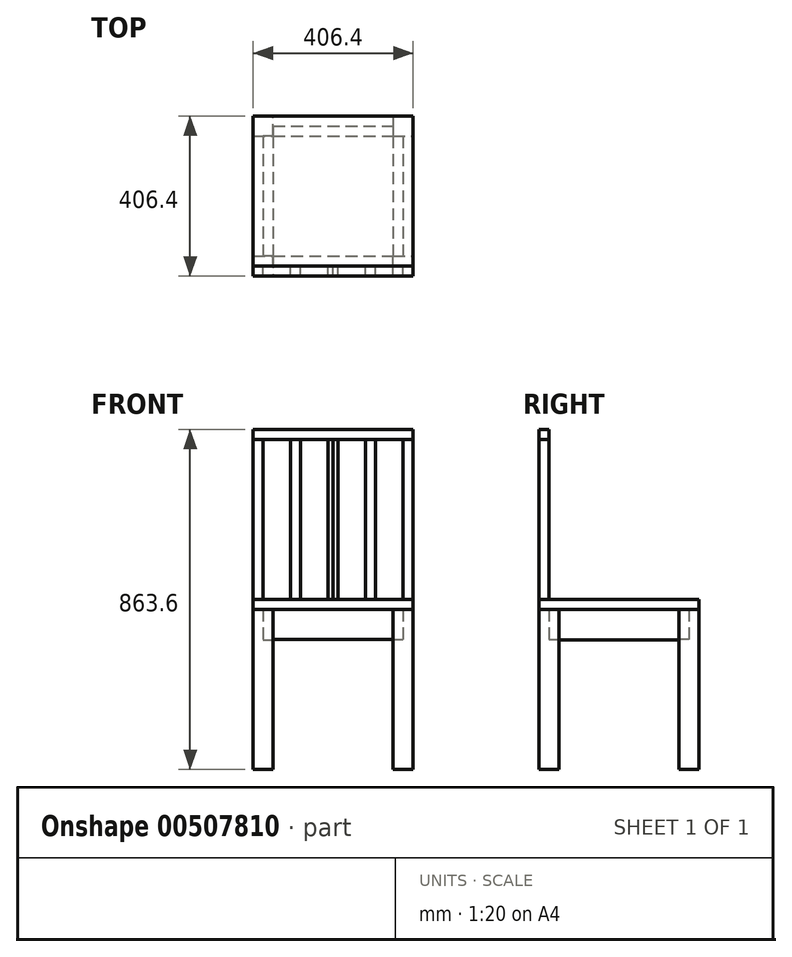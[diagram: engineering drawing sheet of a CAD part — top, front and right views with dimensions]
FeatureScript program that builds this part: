
annotation { "Feature Type Name" : "Feature", "Feature Type Description" : "" }
export const myFeature = defineFeature(function(context is Context, id is Id, definition is map)
    precondition{}
    {
        {
            var Q0;
            Q0=qCreatedBy(makeId("Top.planeOp"),FACE);
            var sketch = newSketch(context, id + "F0", { "sketchPlane" : qUnion([Q0])});
            skLineSegment(sketch, "E0.bottom", {"start": v(0, 0) * mm, "end": v(406.4, 0) * mm});
            skLineSegment(sketch, "E0.top", {"start": v(0, 406.4) * mm, "end": v(406.4, 406.4) * mm});
            skLineSegment(sketch, "E0.left", {"start": v(0, 0) * mm, "end": v(0, 406.4) * mm});
            skLineSegment(sketch, "E0.right", {"start": v(406.4, 0) * mm, "end": v(406.4, 406.4) * mm});
            skPoint(sketch, "E1", {"position": v(0, 50.8) * mm});
            skPoint(sketch, "E2", {"position": v(50.8, 0) * mm});
            skPoint(sketch, "E3", {"position": v(406.4, 50.8) * mm});
            skPoint(sketch, "E4", {"position": v(50.8, 406.4) * mm});
            skPoint(sketch, "E5", {"position": v(0, 355.6) * mm});
            skLineSegment(sketch, "E6", {"start": v(0, 355.6) * mm, "end": v(50.8, 355.6) * mm});
            skLineSegment(sketch, "E7", {"start": v(50.8, 355.6) * mm, "end": v(50.8, 406.4) * mm});
            skPoint(sketch, "E8", {"position": v(355.6, 406.4) * mm});
            skPoint(sketch, "E9", {"position": v(406.4, 355.6) * mm});
            skLineSegment(sketch, "E10", {"start": v(355.6, 406.4) * mm, "end": v(355.6, 355.6) * mm});
            skLineSegment(sketch, "E11", {"start": v(355.6, 355.6) * mm, "end": v(406.4, 355.6) * mm});
            skPoint(sketch, "E12", {"position": v(355.6, 0) * mm});
            skLineSegment(sketch, "E13", {"start": v(355.6, 0) * mm, "end": v(355.6, 50.8) * mm});
            skLineSegment(sketch, "E14", {"start": v(355.6, 50.8) * mm, "end": v(406.4, 50.8) * mm});
            skLineSegment(sketch, "E15", {"start": v(0, 50.8) * mm, "end": v(50.8, 50.8) * mm});
            skLineSegment(sketch, "E16", {"start": v(50.8, 50.8) * mm, "end": v(50.8, 0) * mm});
            skSolve(sketch);
        }
        {
            var Q0;
            {var subQ4=sQuery(id+"F0.wireOp",EDGE,"E15");Q0=makeQuery(id+"F0.imprint","IMPRINT",FACE,{"disambiguationData":[TD([[makeQuery(id+"F0.imprint","IMPRINT",EDGE,{"derivedFrom":subQ4}),-1.0]])]});}
            var Q1;
            {var subQ3=sQuery(id+"F0.wireOp",EDGE,"E13");Q1=makeQuery(id+"F0.imprint","IMPRINT",FACE,{"disambiguationData":[TD([[makeQuery(id+"F0.imprint","IMPRINT",EDGE,{"derivedFrom":subQ3}),-1.0]])]});}
            var Q2;
            {var subQ3=sQuery(id+"F0.wireOp",EDGE,"E10");Q2=makeQuery(id+"F0.imprint","IMPRINT",FACE,{"disambiguationData":[TD([[makeQuery(id+"F0.imprint","IMPRINT",EDGE,{"derivedFrom":subQ3}),1.0]])]});}
            var Q3;
            {var subQ4=sQuery(id+"F0.wireOp",EDGE,"E6");Q3=makeQuery(id+"F0.imprint","IMPRINT",FACE,{"disambiguationData":[TD([[makeQuery(id+"F0.imprint","IMPRINT",EDGE,{"derivedFrom":subQ4}),1.0]])]});}
            extrude(context, id + "F1", {"entities" : qUnion([Q0, Q1, Q2, Q3]), "depth" : 406.4 * mm});
        }
        {
            var Q0;
            Q0=makeQuery(id+"F1.opExtrude","CAP_FACE",FACE,{"disambiguationData":[OSD([sQuery(id+"F0.wireOp",EDGE,"E0.bottom"),sQuery(id+"F0.wireOp",EDGE,"E0.left"),sQuery(id+"F0.wireOp",EDGE,"E15"),sQuery(id+"F0.wireOp",EDGE,"E16")])],"isStart":false});
            var sketch = newSketch(context, id + "F2", { "sketchPlane" : qUnion([Q0])});
            skLineSegment(sketch, "E17.bottom", {"start": v(0, 0) * mm, "end": v(406.4, 0) * mm});
            skLineSegment(sketch, "E17.top", {"start": v(0, 406.4) * mm, "end": v(406.4, 406.4) * mm});
            skLineSegment(sketch, "E17.left", {"start": v(0, 0) * mm, "end": v(0, 406.4) * mm});
            skLineSegment(sketch, "E17.right", {"start": v(406.4, 0) * mm, "end": v(406.4, 406.4) * mm});
            skSolve(sketch);
        }
        {
            var Q0;
            Q0 = qSketchRegion(id + "F2", true);
            extrude(context, id + "F3", {"entities" : qUnion([Q0]), "depth" : 25.4 * mm});
        }
        {
            var Q0;
            Q0=makeQuery(id+"F3.opExtrude","CAP_FACE",FACE,{"disambiguationData":[OSD([sQuery(id+"F2.wireOp",EDGE,"E17.bottom"),sQuery(id+"F2.wireOp",EDGE,"E17.top"),sQuery(id+"F2.wireOp",EDGE,"E17.left"),sQuery(id+"F2.wireOp",EDGE,"E17.right")])],"isStart":false});
            var sketch = newSketch(context, id + "F4", { "sketchPlane" : qUnion([Q0])});
            skLineSegment(sketch, "E18.bottom", {"start": v(0, 0) * mm, "end": v(25.4, 0) * mm});
            skLineSegment(sketch, "E18.top", {"start": v(0, 25.4) * mm, "end": v(25.4, 25.4) * mm});
            skLineSegment(sketch, "E18.left", {"start": v(0, 0) * mm, "end": v(0, 25.4) * mm});
            skLineSegment(sketch, "E18.right", {"start": v(25.4, 0) * mm, "end": v(25.4, 25.4) * mm});
            skLineSegment(sketch, "E19", {"start": v(203.2, 0) * mm, "end": v(203.2, 406.4) * mm});
            skLineSegment(sketch, "E20", {"start": v(25.4, 12.7) * mm, "end": v(95.25, 12.7) * mm});
            skLineSegment(sketch, "E21", {"start": v(203.2, 0) * mm, "end": v(190.5, 0) * mm});
            skLineSegment(sketch, "E22", {"start": v(190.5, 0) * mm, "end": v(190.5, 25.4) * mm});
            skLineSegment(sketch, "E23", {"start": v(190.5, 25.4) * mm, "end": v(203.2, 25.4) * mm});
            skPoint(sketch, "E24.firstSnap0", {"position": v(107.95, 12.7) * mm});
            skLineSegment(sketch, "E24.bottom", {"start": v(107.95, 0) * mm, "end": v(95.25, 0) * mm});
            skLineSegment(sketch, "E24.top", {"start": v(107.95, 25.4) * mm, "end": v(95.25, 25.4) * mm});
            skLineSegment(sketch, "E24.left", {"start": v(107.95, 0) * mm, "end": v(107.95, 25.4) * mm});
            skLineSegment(sketch, "E24.right", {"start": v(95.25, 0) * mm, "end": v(95.25, 25.4) * mm});
            skLineSegment(sketch, "E25.trimOffspring", {"start": v(107.95, 12.7) * mm, "end": v(190.5, 12.7) * mm});
            skLineSegment(sketch, "E26.MirrorCS", {"start": v(107.95, 25.4) * mm, "end": v(120.65, 25.4) * mm});
            skLineSegment(sketch, "E27.MirrorCS", {"start": v(120.65, 0) * mm, "end": v(120.65, 25.4) * mm});
            skLineSegment(sketch, "E28.MirrorCS", {"start": v(107.95, 0) * mm, "end": v(120.65, 0) * mm});
            skSolve(sketch);
        }
        {
            var Q0;
            Q0=makeQuery(id+"F4.imprint","IMPRINT",FACE,{"disambiguationData":[TD([[makeQuery(id+"F4.imprint","IMPRINT",EDGE,{"derivedFrom":sQuery(id+"F4.wireOp",EDGE,"E18.bottom")}),1.0]])]});
            var Q1;
            {var subQ0=sQuery(id+"F4.wireOp",EDGE,"E26.MirrorCS");Q1=makeQuery(id+"F4.imprint","IMPRINT",FACE,{"disambiguationData":[TD([[makeQuery(id+"F4.imprint","IMPRINT",EDGE,{"derivedFrom":subQ0}),-1.0]])]});}
            var Q2;
            {var subQ3=sQuery(id+"F4.wireOp",EDGE,"E24.bottom");Q2=makeQuery(id+"F4.imprint","IMPRINT",FACE,{"disambiguationData":[TD([[makeQuery(id+"F4.imprint","IMPRINT",EDGE,{"derivedFrom":subQ3}),1.0]])]});}
            var Q3;
            {var subQ0=sQuery(id+"F4.wireOp",EDGE,"E28.MirrorCS");Q3=makeQuery(id+"F4.imprint","IMPRINT",FACE,{"disambiguationData":[TD([[makeQuery(id+"F4.imprint","IMPRINT",EDGE,{"derivedFrom":subQ0}),1.0]])]});}
            var Q4;
            {var subQ1=sQuery(id+"F4.wireOp",EDGE,"E21");Q4=makeQuery(id+"F4.imprint","IMPRINT",FACE,{"disambiguationData":[TD([[makeQuery(id+"F4.imprint","IMPRINT",EDGE,{"derivedFrom":subQ1}),1.0]])]});}
            extrude(context, id + "F5", {"entities" : qUnion([Q0, Q1, Q2, Q3, Q4]), "depth" : 406.4 * mm});
        }
        {
            var Q0;
            Q0=makeQuery(id+"F3.opExtrude","CAP_EDGE",EDGE,{"disambiguationData":[OSD([sQuery(id+"F2.wireOp",EDGE,"E17.bottom")])],"isStart":false});
            cPoint(context, id + "F6", {"entities" : qUnion([Q0]), "parameter" : 0.5});
        }
        {
            var Q0;
            Q0=makeQuery(id+"F3.opExtrude","CAP_EDGE",EDGE,{"disambiguationData":[OSD([sQuery(id+"F2.wireOp",EDGE,"E17.top")])],"isStart":false});
            cPoint(context, id + "F7", {"entities" : qUnion([Q0]), "parameter" : 0.5});
        }
        {
            var Q0;
            Q0=makeQuery(id+"F3.opExtrude","CAP_EDGE",EDGE,{"disambiguationData":[OSD([sQuery(id+"F2.wireOp",EDGE,"E17.top")])],"isStart":true});
            cPoint(context, id + "F8", {"entities" : qUnion([Q0]), "parameter" : 0.5});
        }
        {
            var Q0;
            Q0 = qCreatedBy(id + "F6" ,VERTEX);
            var Q1;
            Q1 = qCreatedBy(id + "F7" ,VERTEX);
            var Q2;
            Q2 = qCreatedBy(id + "F8" ,VERTEX);
            cPlane(context, id + "F9", {"entities" : qUnion([Q0, Q1, Q2]), "cplaneType" : CPlaneType.THREE_POINT, "offset" : 25.4 * mm, "width" : 152.4 * mm, "height" : 152.4 * mm});
        }
        {
            var Q0;
            Q0=makeQuery(id+"F5.opExtrude","SWEPT_BODY",BODY,{"disambiguationData":[OSD([sQuery(id+"F4.wireOp",EDGE,"E18.bottom"),sQuery(id+"F4.wireOp",EDGE,"E18.top"),sQuery(id+"F4.wireOp",EDGE,"E18.left"),sQuery(id+"F4.wireOp",EDGE,"E18.right")])]});
            var Q1;
            Q1=makeQuery(id+"F5.opExtrude","SWEPT_BODY",BODY,{"disambiguationData":[OSD([sQuery(id+"F4.wireOp",EDGE,"E24.bottom"),sQuery(id+"F4.wireOp",EDGE,"E24.top"),sQuery(id+"F4.wireOp",EDGE,"E24.right"),sQuery(id+"F4.wireOp",EDGE,"E26.MirrorCS"),sQuery(id+"F4.wireOp",EDGE,"E27.MirrorCS"),sQuery(id+"F4.wireOp",EDGE,"E28.MirrorCS")])]});
            var Q2;
            Q2=makeQuery(id+"F5.opExtrude","SWEPT_BODY",BODY,{"disambiguationData":[OSD([sQuery(id+"F4.wireOp",EDGE,"E19"),sQuery(id+"F4.wireOp",EDGE,"E21"),sQuery(id+"F4.wireOp",EDGE,"E22"),sQuery(id+"F4.wireOp",EDGE,"E23")])]});
            var Q3;
            Q3=qCreatedBy(id+"F9.planeOp",FACE);
            mirror(context, id + "F10", {"entities" : qUnion([Q0, Q1, Q2]), "mirrorPlane" : qUnion([Q3])});
        }
        {
            var Q0;
            Q0=makeQuery(id+"F10.opPattern","COPY",FACE,{"derivedFrom":makeQuery(id+"F5.opExtrude","CAP_FACE",FACE,{"disambiguationData":[OSD([sQuery(id+"F4.wireOp",EDGE,"E18.bottom"),sQuery(id+"F4.wireOp",EDGE,"E18.top"),sQuery(id+"F4.wireOp",EDGE,"E18.left"),sQuery(id+"F4.wireOp",EDGE,"E18.right")])],"isStart":false}),"instanceName":"1"});
            var sketch = newSketch(context, id + "F11", { "sketchPlane" : qUnion([Q0])});
            skLineSegment(sketch, "E29.bottom", {"start": v(0, 0) * mm, "end": v(406.4, 0) * mm});
            skLineSegment(sketch, "E29.top", {"start": v(0, 25.4) * mm, "end": v(406.4, 25.4) * mm});
            skLineSegment(sketch, "E29.left", {"start": v(0, 0) * mm, "end": v(0, 25.4) * mm});
            skLineSegment(sketch, "E29.right", {"start": v(406.4, 0) * mm, "end": v(406.4, 25.4) * mm});
            skSolve(sketch);
        }
        {
            var Q0;
            {var subQ2=sQuery(id+"F11.wireOp",EDGE,"E29.left");Q0=makeQuery(id+"F11.imprint","IMPRINT",FACE,{"disambiguationData":[TD([[makeQuery(id+"F11.imprint","IMPRINT",EDGE,{"derivedFrom":subQ2}),-1.0]])]});}
            var Q1;
            {var subQ0=sQuery(id+"F11.wireOp",EDGE,"E29.right");Q1=makeQuery(id+"F11.imprint","IMPRINT",FACE,{"disambiguationData":[TD([[makeQuery(id+"F11.imprint","IMPRINT",EDGE,{"derivedFrom":subQ0}),1.0]])]});}
            extrude(context, id + "F12", {"entities" : qUnion([Q0, Q1]), "depth" : 25.4 * mm});
        }
        {
            var Q0;
            Q0=makeQuery(id+"F1.opExtrude","SWEPT_FACE",FACE,{"disambiguationData":[OSD([sQuery(id+"F0.wireOp",EDGE,"E14")])]});
            var sketch = newSketch(context, id + "F13", { "sketchPlane" : qUnion([Q0])});
            skLineSegment(sketch, "E30", {"start": v(-381, 406.4) * mm, "end": v(-381, 328.49) * mm});
            skLineSegment(sketch, "E31", {"start": v(-381, 328.49) * mm, "end": v(-355.6, 328.49) * mm});
            skLineSegment(sketch, "E32", {"start": v(-355.6, 328.49) * mm, "end": v(-355.6, 406.4) * mm});
            skLineSegment(sketch, "E33", {"start": v(-355.6, 406.4) * mm, "end": v(-381, 406.4) * mm});
            skSolve(sketch);
        }
        {
            var Q0;
            Q0=makeQuery(id+"F13.imprint","IMPRINT",FACE,{"disambiguationData":[TD([[makeQuery(id+"F13.imprint","IMPRINT",EDGE,{"derivedFrom":sQuery(id+"F13.wireOp",EDGE,"E30")}),1.0]])]});
            extrude(context, id + "F14", {"entities" : qUnion([Q0]), "depth" : 304.8 * mm});
        }
        {
            var Q0;
            Q0=makeQuery(id+"F14.opExtrude","SWEPT_BODY",BODY,{"disambiguationData":[OSD([sQuery(id+"F13.wireOp",EDGE,"E30"),sQuery(id+"F13.wireOp",EDGE,"E31"),sQuery(id+"F13.wireOp",EDGE,"E32"),sQuery(id+"F13.wireOp",EDGE,"E33")])]});
            var Q1;
            Q1=qCreatedBy(id+"F9.planeOp",FACE);
            mirror(context, id + "F15", {"entities" : qUnion([Q0]), "mirrorPlane" : qUnion([Q1])});
        }
        {
            var Q0;
            Q0=makeQuery(id+"F1.opExtrude","SWEPT_FACE",FACE,{"disambiguationData":[OSD([sQuery(id+"F0.wireOp",EDGE,"E10")])]});
            var sketch = newSketch(context, id + "F16", { "sketchPlane" : qUnion([Q0])});
            skLineSegment(sketch, "E34", {"start": v(-355.6, 406.4) * mm, "end": v(-381, 406.4) * mm});
            skLineSegment(sketch, "E35", {"start": v(-381, 406.4) * mm, "end": v(-381, 330.2) * mm});
            skLineSegment(sketch, "E36", {"start": v(-381, 330.2) * mm, "end": v(-355.6, 330.2) * mm});
            skLineSegment(sketch, "E37", {"start": v(-355.6, 330.2) * mm, "end": v(-355.6, 406.4) * mm});
            skLineSegment(sketch, "E38", {"start": v(-355.6, 330.2) * mm, "end": v(-50.8, 330.2) * mm});
            skLineSegment(sketch, "E39", {"start": v(-203.2, 330.2) * mm, "end": v(-203.2, 388.6) * mm});
            skLineSegment(sketch, "E40.MirrorCS", {"start": v(-50.8, 330.2) * mm, "end": v(-50.8, 406.4) * mm});
            skLineSegment(sketch, "E41.MirrorCS", {"start": v(-25.4, 330.2) * mm, "end": v(-50.8, 330.2) * mm});
            skLineSegment(sketch, "E42.MirrorCS", {"start": v(-50.8, 406.4) * mm, "end": v(-25.4, 406.4) * mm});
            skLineSegment(sketch, "E43.MirrorCS", {"start": v(-25.4, 406.4) * mm, "end": v(-25.4, 330.2) * mm});
            skSolve(sketch);
        }
        {
            var Q0;
            Q0=makeQuery(id+"F16.imprint","IMPRINT",FACE,{"disambiguationData":[TD([[makeQuery(id+"F16.imprint","IMPRINT",EDGE,{"derivedFrom":sQuery(id+"F16.wireOp",EDGE,"E34")}),-1.0]])]});
            var Q1;
            Q1=makeQuery(id+"F16.imprint","IMPRINT",FACE,{"disambiguationData":[TD([[makeQuery(id+"F16.imprint","IMPRINT",EDGE,{"derivedFrom":sQuery(id+"F16.wireOp",EDGE,"E40.MirrorCS")}),-1.0]])]});
            extrude(context, id + "F17", {"entities" : qUnion([Q0, Q1]), "depth" : 304.8 * mm});
        }
    });
